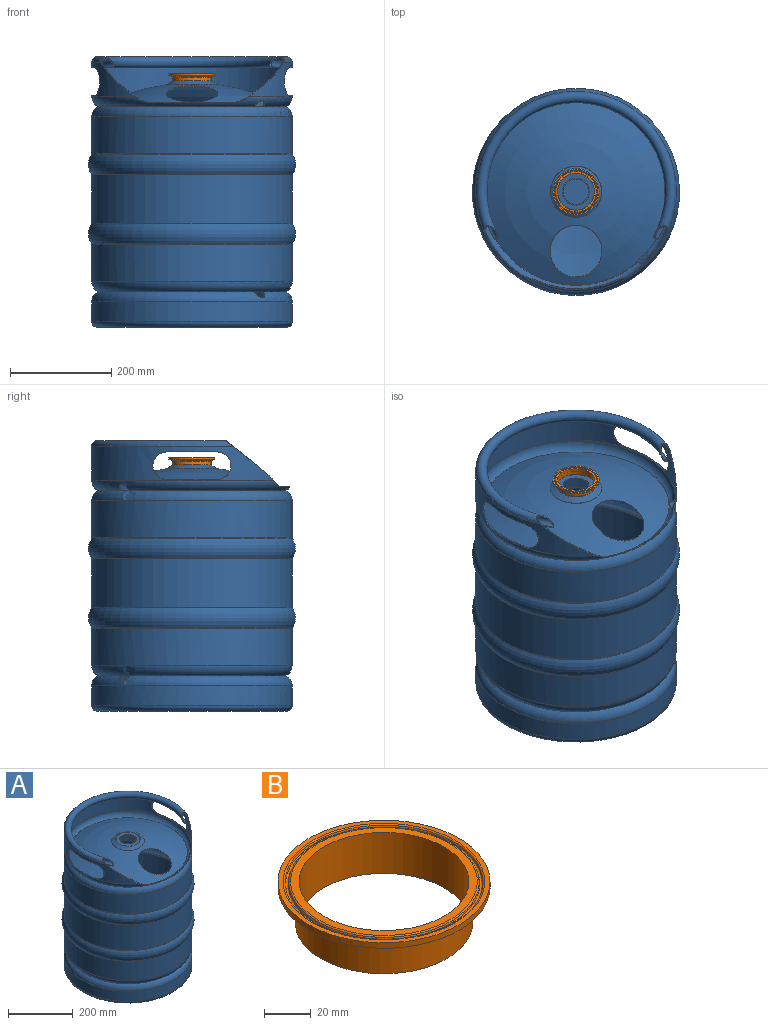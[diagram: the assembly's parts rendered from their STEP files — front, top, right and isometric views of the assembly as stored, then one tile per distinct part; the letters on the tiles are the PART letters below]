
ASSEMBLY  parts=2 mates=1
PART A: 77 faces, bbox 441.7x441.7x533.1 mm
  f0: torus R=26.7mm, axis (0,0,1), area 394.6mm2, adj f1,f76
  f1: plane 72.5x72.5mm, normal (0,0,-1), area 1888.4mm2, adj f0,f4
  f2: torus R=186.5mm, axis (0,0,1), area 32524.2mm2, adj f3,f6,f70,f71
  f3: cylinder r=186.5mm len=373mm, axis (0,0,1), area 1330.1mm2, adj f2,f11,f70,f71
  f4: torus R=36.25mm, axis (0,0,1), area 203.1mm2, adj f1,f16
  f5: cone r=44.04mm half-angle=60.3deg, axis (0,0,-1), area 4143.2mm2, adj f17,f76
  f6: cylinder r=195.8mm len=391.6mm, axis (0,0,1), area 43957.3mm2, adj f2,f7,f8,f9,f10,f12,f13,f14
  f7: plane 100x8.19mm, normal (0,0,-1), area 171.9mm2, adj f6,f8,f10,f19
  f8: cylinder r=27mm len=54mm, axis (1,0,0), area 153.6mm2, adj f6,f7,f9,f19
  f9: plane 100x8.19mm, normal (0,0,1), area 171.9mm2, adj f6,f8,f10,f19
  f10: cylinder r=27mm len=54mm, axis (1,0,0), area 153.6mm2, adj f6,f7,f9,f19
  f11: torus R=186.5mm, axis (0,0,1), area 38367.4mm2, adj f3,f19,f70,f71
  f12: cylinder r=27mm len=54mm, axis (1,0,0), area 153.7mm2, adj f6,f13,f15,f19
  f13: plane 100x8.19mm, normal (0,0,-1), area 171.9mm2, adj f6,f12,f14,f19
  f14: cylinder r=27mm len=54mm, axis (1,0,0), area 153.7mm2, adj f6,f13,f15,f19
  f15: plane 100x8.19mm, normal (0,0,1), area 171.9mm2, adj f6,f12,f14,f19
  f16: cone r=43.4mm half-angle=60.3deg, axis (0,0,-1), area 3961mm2, adj f4,f22
  f17: sphere r=394.17mm, area 95625.7mm2, adj f5,f18,f20,f23,f75
  f18: torus R=174.61mm, axis (0,0,1), area 24774.9mm2, adj f6,f17,f21,f24,f72,f73,f74
  f19: cylinder r=197.5mm len=395mm, axis (0,0,1), area 43642.4mm2, adj f7,f8,f9,f10,f11,f12,f13,f14
  f20: torus R=174.61mm, axis (0,0,1), area 54.5mm2, adj f17,f21,f28
  f21: cylinder r=12mm len=27.54mm, axis (-0.71,0.71,0), area 84.3mm2, adj f18,f20,f25,f27,f28
  f22: torus R=50.55mm, axis (0,0,1), area 208.2mm2, adj f16,f28
  f23: torus R=174.61mm, axis (0,0,1), area 54.5mm2, adj f17,f24,f28
  f24: cylinder r=12mm len=27.54mm, axis (-0.71,0.71,0), area 84.4mm2, adj f18,f23,f26,f27,f28
  f25: plane 19.59x19.59mm, normal (0,0,1), area 88.9mm2, adj f21,f28,f29
  f26: plane 19.59x19.59mm, normal (0,0,1), area 88.9mm2, adj f24,f28,f29
  f27: torus R=174.61mm, axis (0,0,1), area 26376.8mm2, adj f19,f21,f24,f29,f72,f73,f74
  f28: sphere r=392.24mm, area 95604.2mm2, adj f20,f21,f22,f23,f24,f25,f26,f30
  f29: torus R=174.61mm, axis (0,0,1), area 30051.2mm2, adj f25,f26,f27,f31
  f30: torus R=174.61mm, axis (0,0,1), area 28321.6mm2, adj f28,f32
  f31: cylinder r=197.5mm len=395mm, axis (0,0,1), area 90908mm2, adj f29,f33
  f32: cylinder r=195.8mm len=391.6mm, axis (0,0,1), area 90923.1mm2, adj f30,f34
  f33: torus R=199.2mm, axis (0,0,1), area 1293.5mm2, adj f31,f35
  f34: torus R=197.5mm, axis (0,0,1), area 1280.4mm2, adj f32,f36
  f35: torus R=169.98mm, axis (0,0,1), area 52897mm2, adj f33,f37
  f36: torus R=168.18mm, axis (0,0,1), area 52533.6mm2, adj f34,f38
  f37: torus R=199.2mm, axis (0,0,1), area 1293.5mm2, adj f35,f39
  f38: torus R=197.5mm, axis (0,0,1), area 1280.4mm2, adj f36,f40
  f39: cylinder r=197.5mm len=395mm, axis (0,0,1), area 119017.3mm2, adj f37,f41
  f40: cylinder r=195.8mm len=391.6mm, axis (0,0,1), area 117827.7mm2, adj f38,f42
  f41: torus R=199.2mm, axis (0,0,1), area 1293.5mm2, adj f39,f43
  f42: torus R=197.5mm, axis (0,0,1), area 1280.4mm2, adj f40,f44
  f43: torus R=169.98mm, axis (0,0,1), area 52897mm2, adj f41,f46
  f44: torus R=168.18mm, axis (0,0,1), area 52533.6mm2, adj f42,f47
  f45: cylinder r=186.5mm len=373mm, axis (0,0,1), area 1992.1mm2, adj f48,f49
  f46: torus R=199.2mm, axis (0,0,1), area 1293.5mm2, adj f43,f50
  f47: torus R=197.5mm, axis (0,0,1), area 1280.4mm2, adj f44,f52
  f48: torus R=186.5mm, axis (0,0,1), area 50811.6mm2, adj f45,f57
  f49: torus R=186.5mm, axis (0,0,1), area 59982.2mm2, adj f45,f58
  f50: cylinder r=197.5mm len=395mm, axis (0,0,1), area 90908mm2, adj f46,f59
  f51: plane 115.75x115.75mm, normal (0,0,1), area 10522.4mm2, adj f60
  f52: cylinder r=195.8mm len=391.6mm, axis (0,0,1), area 90923.1mm2, adj f47,f61
  f53: cylinder r=12mm len=27.54mm, axis (-0.71,0.71,0), area 84.4mm2, adj f54,f56,f63,f64,f66
  f54: plane 19.59x19.59mm, normal (0,0,-1), area 88.9mm2, adj f53,f59,f66
  f55: plane 116.04x116.04mm, normal (0,0,-1), area 10574.7mm2, adj f62
  f56: torus R=174.61mm, axis (0,0,1), area 54.5mm2, adj f53,f66,f67
  f57: cylinder r=195.8mm len=391.6mm, axis (0,0,1), area 48533.7mm2, adj f48,f63
  f58: cylinder r=197.5mm len=395mm, axis (0,0,1), area 48151.7mm2, adj f49,f64
  f59: torus R=174.61mm, axis (0,0,1), area 30051.2mm2, adj f50,f54,f64,f65
  f60: torus R=57.87mm, axis (0,0,1), area 92.1mm2, adj f51,f66
  f61: torus R=174.61mm, axis (0,0,1), area 28321.6mm2, adj f52,f66
  f62: torus R=58.02mm, axis (0,0,1), area 92.2mm2, adj f55,f67
  f63: torus R=174.61mm, axis (0,0,1), area 27576.7mm2, adj f53,f57,f67,f68
  f64: torus R=174.61mm, axis (0,0,1), area 29406.9mm2, adj f53,f58,f59,f68
  f65: plane 19.59x19.59mm, normal (0,0,-1), area 88.9mm2, adj f59,f66,f68
  f66: sphere r=392.24mm, area 101532.6mm2, adj f53,f54,f56,f60,f61,f65,f68,f69
  f67: sphere r=394.17mm, area 101563.9mm2, adj f56,f62,f63,f69
  f68: cylinder r=12mm len=27.54mm, axis (-0.71,0.71,0), area 84.3mm2, adj f63,f64,f65,f66,f69
  f69: torus R=174.61mm, axis (0,0,1), area 54.5mm2, adj f66,f67,f68
  f70: plane 82.65x65.66mm, normal (0,-0.62,0.78), area 333.4mm2, adj f2,f3,f6,f11,f19,f73
  f71: plane 82.65x65.66mm, normal (0,-0.62,0.78), area 333.3mm2, adj f2,f3,f6,f11,f19,f74
  f72: plane 174.26x20.77mm, normal (0,0,1), area 370mm2, adj f18,f27,f73,f74
  f73: plane 46.41x25.32mm, normal (0,-0.74,0.67), area 108mm2, adj f6,f18,f19,f27,f70,f72
  f74: plane 46.41x25.32mm, normal (0,-0.74,0.67), area 108mm2, adj f6,f18,f19,f27,f71,f72
  f75: cylinder r=51mm len=102mm, axis (0,0,1), area 581.6mm2, adj f17,f28
  f76: plane 75.14x75.14mm, normal (0,0,1), area 2462.1mm2, adj f0,f5
PART B: 13 faces, bbox 94.8x94.8x21.5 mm
  f0: plane 91x91mm, normal (0,0,1), area 626.9mm2, adj f1,f12
  f1: torus R=43.25mm, axis (0,0,-1), area 246.8mm2, adj f0,f2
  f2: cone r=42.22mm half-angle=23deg, axis (0,0,1), area 213.6mm2, adj f1,f3
  f3: torus R=41.67mm, axis (0,0,-1), area 365.5mm2, adj f2,f4
  f4: cone r=41.12mm half-angle=23deg, axis (0,0,-1), area 206.5mm2, adj f3,f5
  f5: torus R=40.08mm, axis (0,0,-1), area 233.2mm2, adj f4,f6
  f6: plane 80.16x80.16mm, normal (0,0,1), area 873.3mm2, adj f5,f7
  f7: cylinder r=36.45mm len=72.9mm, axis (0,0,-1), area 4924mm2, adj f6,f8
  f8: plane 76.2x76.2mm, normal (0,0,-1), area 386.4mm2, adj f7,f9
  f9: cylinder r=38.1mm len=76.2mm, axis (0,0,-1), area 3583.6mm2, adj f8,f10
  f10: torus R=39.2mm, axis (0,0,-1), area 318mm2, adj f9,f11
  f11: cone r=45.5mm half-angle=68.8deg, axis (0,0,1), area 1903.5mm2, adj f10,f12
  f12: cylinder r=45.5mm len=91mm, axis (0,0,-1), area 829.1mm2, adj f0,f11
PLACE A t=(-69.13,-25.95,-246.66)mm fixed
PLACE B rot(axis=(1,0,0),0deg) t=(-69.13,-25.95,231.4)mm
MATE slider A.f37 <-> B.f1  axis (0,0,-1) through (-69.13,-25.95,231.4)mm
